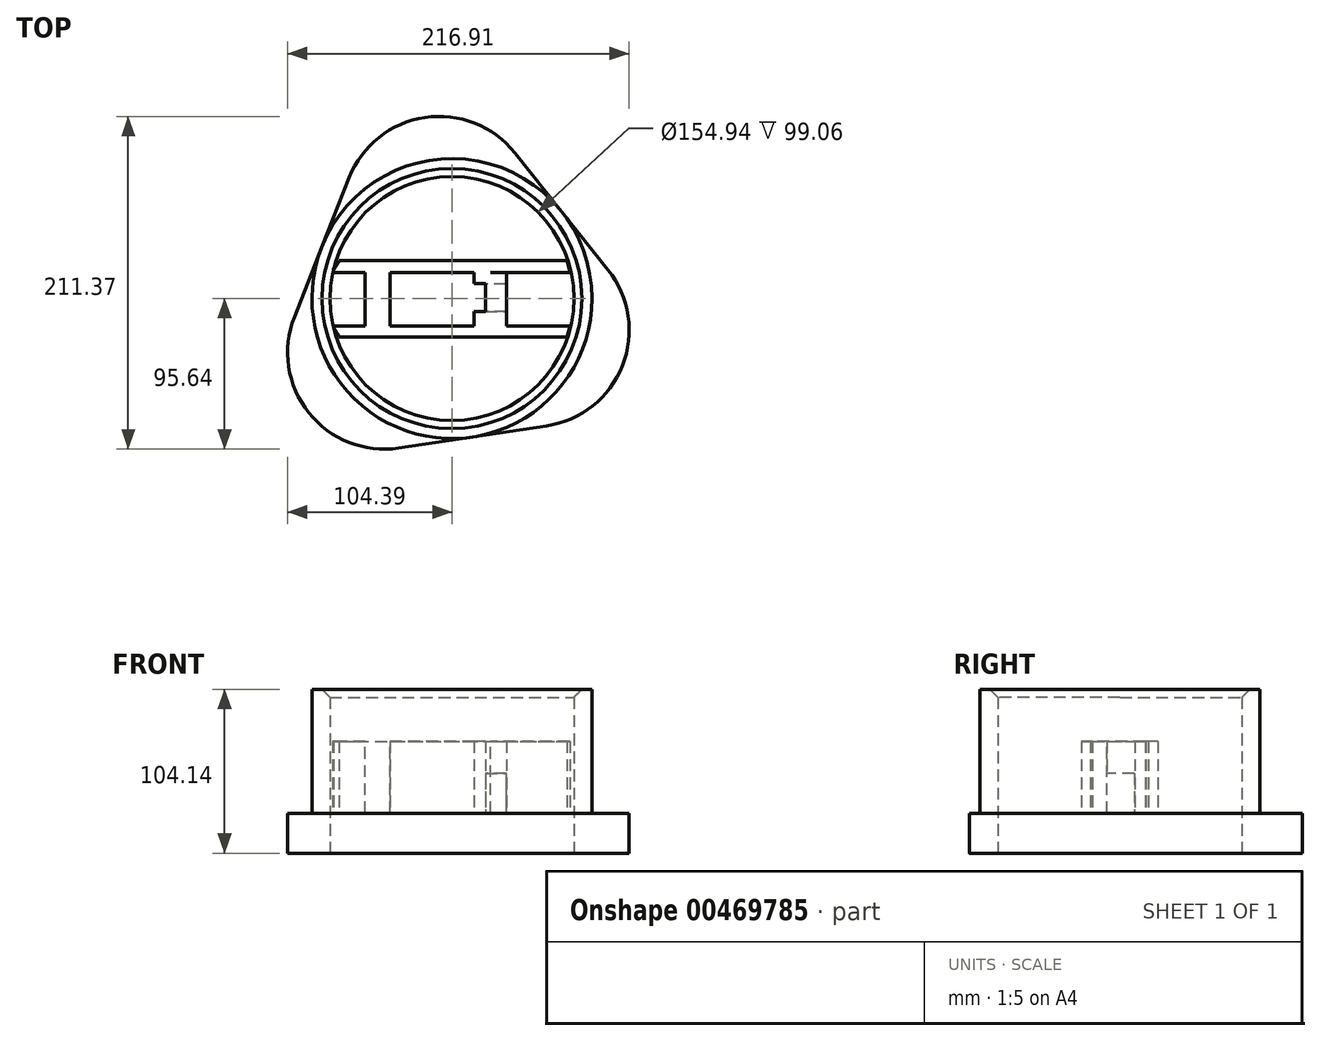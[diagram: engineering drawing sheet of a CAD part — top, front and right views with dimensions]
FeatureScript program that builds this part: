
annotation { "Feature Type Name" : "Feature", "Feature Type Description" : "" }
export const myFeature = defineFeature(function(context is Context, id is Id, definition is map)
    precondition{}
    {
        {
            var Q0;
            Q0=qCreatedBy(makeId("Top.planeOp"),FACE);
            var sketch = newSketch(context, id + "F0", { "sketchPlane" : qUnion([Q0])});
            skCircle(sketch, "E0", {"center": v(0, 0) * mm, "radius": 88.9 * mm});
            skCircle(sketch, "E1", {"center": v(0, 0) * mm, "radius": 77.47 * mm});
            skSolve(sketch);
        }
        {
            var Q0;
            Q0=qCreatedBy(makeId("Top.planeOp"),FACE);
            var sketch = newSketch(context, id + "F1", { "sketchPlane" : qUnion([Q0])});
            skLineSegment(sketch, "E2", {"start": v(-71.86, 24.18) * mm, "end": v(73.2, 24.18) * mm});
            skLineSegment(sketch, "E3", {"start": v(-71.86, -24.51) * mm, "end": v(73.2, -24.51) * mm});
            skLineSegment(sketch, "E4", {"start": v(-71.86, 16.45) * mm, "end": v(74.88, 16.45) * mm});
            skLineSegment(sketch, "E5", {"start": v(74.88, 16.45) * mm, "end": v(-76.22, 16.45) * mm});
            skLineSegment(sketch, "E6", {"start": v(-71.86, 24.18) * mm, "end": v(-76.22, 16.45) * mm});
            skLineSegment(sketch, "E7", {"start": v(73.2, 24.18) * mm, "end": v(74.88, 16.45) * mm});
            skLineSegment(sketch, "E8", {"start": v(-71.86, -17.46) * mm, "end": v(74.88, -17.46) * mm});
            skLineSegment(sketch, "E9", {"start": v(74.88, -17.46) * mm, "end": v(-75.88, -17.46) * mm});
            skLineSegment(sketch, "E10", {"start": v(-71.86, -24.51) * mm, "end": v(-75.88, -17.46) * mm});
            skLineSegment(sketch, "E11", {"start": v(74.88, -17.46) * mm, "end": v(73.2, -24.51) * mm});
            skSolve(sketch);
        }
        {
            var Q0;
            Q0=makeQuery(id+"F0.imprint","IMPRINT",FACE,{"disambiguationData":[TD([[makeQuery(id+"F0.imprint","IMPRINT",EDGE,{"derivedFrom":sQuery(id+"F0.wireOp",EDGE,"E0")}),1.0]])]});
            extrude(context, id + "F2", {"entities" : qUnion([Q0]), "depth" : 78.74 * mm});
        }
        {
            var Q0;
            Q0=makeQuery(id+"F1.imprint","IMPRINT",FACE,{"disambiguationData":[TD([[makeQuery(id+"F1.imprint","IMPRINT",EDGE,{"derivedFrom":sQuery(id+"F1.wireOp",EDGE,"E2")}),-1.0]])]});
            var Q1;
            Q1=makeQuery(id+"F1.imprint","IMPRINT",FACE,{"disambiguationData":[TD([[makeQuery(id+"F1.imprint","IMPRINT",EDGE,{"derivedFrom":sQuery(id+"F1.wireOp",EDGE,"E3")}),1.0]])]});
            extrude(context, id + "F3", {"entities" : qUnion([Q0, Q1]), "operationType" : NewBodyOperationType.ADD, "depth" : 45.72 * mm});
        }
        {
            var Q0;
            Q0=makeQuery(id+"F2.opExtrude","CAP_EDGE",EDGE,{"disambiguationData":[OSD([sQuery(id+"F0.wireOp",EDGE,"E1")])],"isStart":false});
            chamfer(context, id + "F4", {"entities" : qUnion([Q0]), "width" : 5.08 * mm, "tangentPropagation" : true});
        }
        {
            var Q0;
            Q0=qCreatedBy(makeId("Top.planeOp"),FACE);
            var sketch = newSketch(context, id + "F5", { "sketchPlane" : qUnion([Q0])});
            skLineSegment(sketch, "E12", {"start": v(-55.07, 16.12) * mm, "end": v(-55.07, -16.45) * mm});
            skLineSegment(sketch, "E13", {"start": v(-39.29, 16.12) * mm, "end": v(-39.29, -17.12) * mm});
            skLineSegment(sketch, "E14", {"start": v(-55.07, -16.45) * mm, "end": v(-55.07, -18.16) * mm});
            skLineSegment(sketch, "E15", {"start": v(-55.07, -18.16) * mm, "end": v(-39.25, -18.84) * mm});
            skLineSegment(sketch, "E16", {"start": v(-39.25, -18.84) * mm, "end": v(-39.29, 17.9) * mm});
            skLineSegment(sketch, "E17", {"start": v(-39.29, 17.9) * mm, "end": v(-55.07, 18.58) * mm});
            skLineSegment(sketch, "E18", {"start": v(-55.07, 18.58) * mm, "end": v(-55.07, 10.55) * mm});
            skSolve(sketch);
        }
        {
            var Q0;
            {var subQ0=sQuery(id+"F5.wireOp",EDGE,"E12");Q0=makeQuery(id+"F5.imprint","IMPRINT",FACE,{"disambiguationData":[TD([[makeQuery(id+"F5.imprint","IMPRINT",EDGE,{"derivedFrom":subQ0}),1.0]])]});}
            extrude(context, id + "F6", {"entities" : qUnion([Q0]), "operationType" : NewBodyOperationType.ADD, "depth" : 45.72 * mm});
        }
        {
            var Q0;
            Q0=qCreatedBy(makeId("Top.planeOp"),FACE);
            var sketch = newSketch(context, id + "F7", { "sketchPlane" : qUnion([Q0])});
            skLineSegment(sketch, "E19", {"start": v(34.58, 16.12) * mm, "end": v(34.58, -16.45) * mm});
            skLineSegment(sketch, "E20", {"start": v(14.1, -16.45) * mm, "end": v(14.1, 16.79) * mm});
            skLineSegment(sketch, "E21", {"start": v(14.1, 16.79) * mm, "end": v(34.58, 16.12) * mm});
            skLineSegment(sketch, "E22", {"start": v(34.58, -22.83) * mm, "end": v(14.1, -22.83) * mm});
            skLineSegment(sketch, "E23", {"start": v(14.1, -22.83) * mm, "end": v(14.1, -12.09) * mm});
            skLineSegment(sketch, "E24", {"start": v(34.58, -16.45) * mm, "end": v(34.58, -22.83) * mm});
            skSolve(sketch);
        }
        {
            var Q0;
            Q0=makeQuery(id+"F7.imprint","IMPRINT",FACE,{"disambiguationData":[TD([[makeQuery(id+"F7.imprint","IMPRINT",EDGE,{"derivedFrom":sQuery(id+"F7.wireOp",EDGE,"E19")}),-1.0]])]});
            extrude(context, id + "F8", {"entities" : qUnion([Q0]), "operationType" : NewBodyOperationType.ADD, "depth" : 45.72 * mm});
        }
        {
            var Q0;
            Q0=qCreatedBy(makeId("Top.planeOp"),FACE);
            var sketch = newSketch(context, id + "F9", { "sketchPlane" : qUnion([Q0])});
            skLineSegment(sketch, "E25", {"start": v(13.77, 9.4) * mm, "end": v(21.15, 9.4) * mm});
            skLineSegment(sketch, "E26", {"start": v(21.15, 9.4) * mm, "end": v(21.15, -8.4) * mm});
            skLineSegment(sketch, "E27", {"start": v(21.15, -8.4) * mm, "end": v(13.77, -8.4) * mm});
            skLineSegment(sketch, "E28", {"start": v(13.77, 9.4) * mm, "end": v(13.77, -8.4) * mm});
            skSolve(sketch);
        }
        {
            var Q0;
            Q0=makeQuery(id+"F9.imprint","IMPRINT",FACE,{"disambiguationData":[TD([[makeQuery(id+"F9.imprint","IMPRINT",EDGE,{"derivedFrom":sQuery(id+"F9.wireOp",EDGE,"E25")}),-1.0]])]});
            extrude(context, id + "F10", {"entities" : qUnion([Q0]), "operationType" : NewBodyOperationType.REMOVE, "depth" : 88.4 * mm});
        }
        {
            var Q0;
            Q0=qCreatedBy(makeId("Top.planeOp"),FACE);
            var sketch = newSketch(context, id + "F11", { "sketchPlane" : qUnion([Q0])});
            skLineSegment(sketch, "E29", {"start": v(20.82, -8.4) * mm, "end": v(34.25, -8.4) * mm});
            skLineSegment(sketch, "E30", {"start": v(34.25, 9.07) * mm, "end": v(21.15, 9.07) * mm});
            skLineSegment(sketch, "E31", {"start": v(21.15, 9.07) * mm, "end": v(20.82, -8.4) * mm});
            skLineSegment(sketch, "E32", {"start": v(34.25, -8.4) * mm, "end": v(41.33, -8.4) * mm});
            skLineSegment(sketch, "E33", {"start": v(41.33, -8.4) * mm, "end": v(41.33, 8.9) * mm});
            skLineSegment(sketch, "E34", {"start": v(41.33, 8.9) * mm, "end": v(34.25, 9.07) * mm});
            skSolve(sketch);
        }
        {
            var Q0;
            Q0=makeQuery(id+"F11.imprint","IMPRINT",FACE,{"disambiguationData":[TD([[makeQuery(id+"F11.imprint","IMPRINT",EDGE,{"derivedFrom":sQuery(id+"F11.wireOp",EDGE,"E29")}),1.0]])]});
            extrude(context, id + "F12", {"entities" : qUnion([Q0]), "operationType" : NewBodyOperationType.REMOVE, "depth" : 25.4 * mm});
        }
        {
            var Q0;
            Q0=makeQuery(id+"F8.boolean.opBoolean","MERGE",FACE,{"derivedFrom":[makeQuery(id+"F6.boolean.opBoolean","MERGE",FACE,{"derivedFrom":[makeQuery(id+"F3.boolean.opBoolean","MERGE",FACE,{"derivedFrom":[makeQuery(id+"F2.opExtrude","CAP_FACE",FACE,{"disambiguationData":[OSD([sQuery(id+"F0.wireOp",EDGE,"E0"),sQuery(id+"F0.wireOp",EDGE,"E1")])],"isStart":true}),makeQuery(id+"F3.opExtrude","CAP_FACE",FACE,{"disambiguationData":[OSD([sQuery(id+"F1.wireOp",EDGE,"E2"),sQuery(id+"F1.wireOp",EDGE,"E5"),sQuery(id+"F1.wireOp",EDGE,"E6"),sQuery(id+"F1.wireOp",EDGE,"E7")])],"isStart":true}),makeQuery(id+"F3.opExtrude","CAP_FACE",FACE,{"disambiguationData":[OSD([sQuery(id+"F1.wireOp",EDGE,"E3"),sQuery(id+"F1.wireOp",EDGE,"E9"),sQuery(id+"F1.wireOp",EDGE,"E10"),sQuery(id+"F1.wireOp",EDGE,"E11")])],"isStart":true})]}),makeQuery(id+"F6.opExtrude","CAP_FACE",FACE,{"disambiguationData":[OSD([sQuery(id+"F5.wireOp",EDGE,"E12"),sQuery(id+"F5.wireOp",EDGE,"E14"),sQuery(id+"F5.wireOp",EDGE,"E15"),sQuery(id+"F5.wireOp",EDGE,"E16"),sQuery(id+"F5.wireOp",EDGE,"E17"),sQuery(id+"F5.wireOp",EDGE,"E18")])],"isStart":true})]}),makeQuery(id+"F8.opExtrude","CAP_FACE",FACE,{"disambiguationData":[OSD([sQuery(id+"F7.wireOp",EDGE,"E19"),sQuery(id+"F7.wireOp",EDGE,"E20"),sQuery(id+"F7.wireOp",EDGE,"E21"),sQuery(id+"F7.wireOp",EDGE,"E22"),sQuery(id+"F7.wireOp",EDGE,"E23"),sQuery(id+"F7.wireOp",EDGE,"E24")])],"isStart":true})]});
            var sketch = newSketch(context, id + "F13", { "sketchPlane" : qUnion([Q0])});
            skCircle(sketch, "E35", {"center": v(0, 0) * mm, "radius": 88.9 * mm});
            skCircle(sketch, "E36.cCircle", {"center": v(0, 0) * mm, "radius": 88.9 * mm, "construction": true});
            skLineSegment(sketch, "E36.0", {"start": v(-139.09, 110.76) * mm, "end": v(165.46, 65.08) * mm});
            skLineSegment(sketch, "E36.1", {"start": v(165.46, 65.08) * mm, "end": v(-26.37, -175.83) * mm});
            skLineSegment(sketch, "E36.2", {"start": v(-26.37, -175.83) * mm, "end": v(-139.09, 110.76) * mm});
            skPoint(sketch, "E36.0.midPoint", {"position": v(13.19, 87.92) * mm});
            skCircle(sketch, "E37", {"center": v(0, 0) * mm, "radius": 77.47 * mm});
            skSolve(sketch);
        }
        {
            var Q0;
            {var subQ17=sQuery(id+"F13.wireOp",EDGE,"E35");var subQ20=makeQuery(id+"F13.imprint","INTERSECT",VERTEX,{"derivedFrom":[subQ17,sQuery(id+"F13.wireOp",EDGE,"E36.2")]});Q0=makeQuery(id+"F13.imprint","IMPRINT",FACE,{"disambiguationData":[TD([[makeQuery(id+"F13.imprint","IMPRINT",EDGE,{"disambiguationData":[TD([[subQ20,1.0]])],"derivedFrom":subQ17}),-1.0]])]});}
            var Q1;
            {var subQ0=sQuery(id+"F13.wireOp",EDGE,"E36.2");var subQ1=sQuery(id+"F13.wireOp",EDGE,"E35");var subQ2=makeQuery(id+"F13.imprint","INTERSECT",VERTEX,{"derivedFrom":[subQ1,subQ0]});Q1=makeQuery(id+"F13.imprint","IMPRINT",FACE,{"disambiguationData":[TD([[makeQuery(id+"F13.imprint","IMPRINT",EDGE,{"disambiguationData":[TD([[subQ2,-1.0]])],"derivedFrom":subQ1}),1.0]])]});}
            var Q2;
            {var subQ0=sQuery(id+"F13.wireOp",EDGE,"E36.1");var subQ1=sQuery(id+"F13.wireOp",EDGE,"E35");var subQ2=makeQuery(id+"F13.imprint","INTERSECT",VERTEX,{"derivedFrom":[subQ1,subQ0]});Q2=makeQuery(id+"F13.imprint","IMPRINT",FACE,{"disambiguationData":[TD([[makeQuery(id+"F13.imprint","IMPRINT",EDGE,{"disambiguationData":[TD([[subQ2,1.0]])],"derivedFrom":subQ1}),1.0]])]});}
            var Q3;
            {var subQ0=sQuery(id+"F13.wireOp",EDGE,"E36.2");var subQ1=sQuery(id+"F13.wireOp",EDGE,"E35");var subQ2=makeQuery(id+"F13.imprint","INTERSECT",VERTEX,{"derivedFrom":[subQ1,subQ0]});Q3=makeQuery(id+"F13.imprint","IMPRINT",FACE,{"disambiguationData":[TD([[makeQuery(id+"F13.imprint","IMPRINT",EDGE,{"disambiguationData":[TD([[subQ2,1.0]])],"derivedFrom":subQ1}),1.0]])]});}
            extrude(context, id + "F14", {"entities" : qUnion([Q0, Q1, Q2, Q3]), "operationType" : NewBodyOperationType.ADD, "depth" : 25.4 * mm});
        }
        {
            var Q0;
            Q0=makeQuery(id+"F14.opExtrude","SWEPT_EDGE",EDGE,{"disambiguationData":[OSD([sQuery(id+"F13.wireOp",EDGE,"E36.0"),sQuery(id+"F13.wireOp",EDGE,"E36.1")])]});
            var Q1;
            Q1=makeQuery(id+"F14.opExtrude","SWEPT_EDGE",EDGE,{"disambiguationData":[OSD([sQuery(id+"F13.wireOp",EDGE,"E36.0"),sQuery(id+"F13.wireOp",EDGE,"E36.2")])]});
            var Q2;
            Q2=makeQuery(id+"F14.opExtrude","SWEPT_EDGE",EDGE,{"disambiguationData":[OSD([sQuery(id+"F13.wireOp",EDGE,"E36.1"),sQuery(id+"F13.wireOp",EDGE,"E36.2")])]});
            fillet(context, id + "F15", {"entities" : qUnion([Q0, Q1, Q2]), "radius" : 61.47 * mm, "tangentPropagation" : true, "allowEdgeOverflow" : false});
        }
    });
